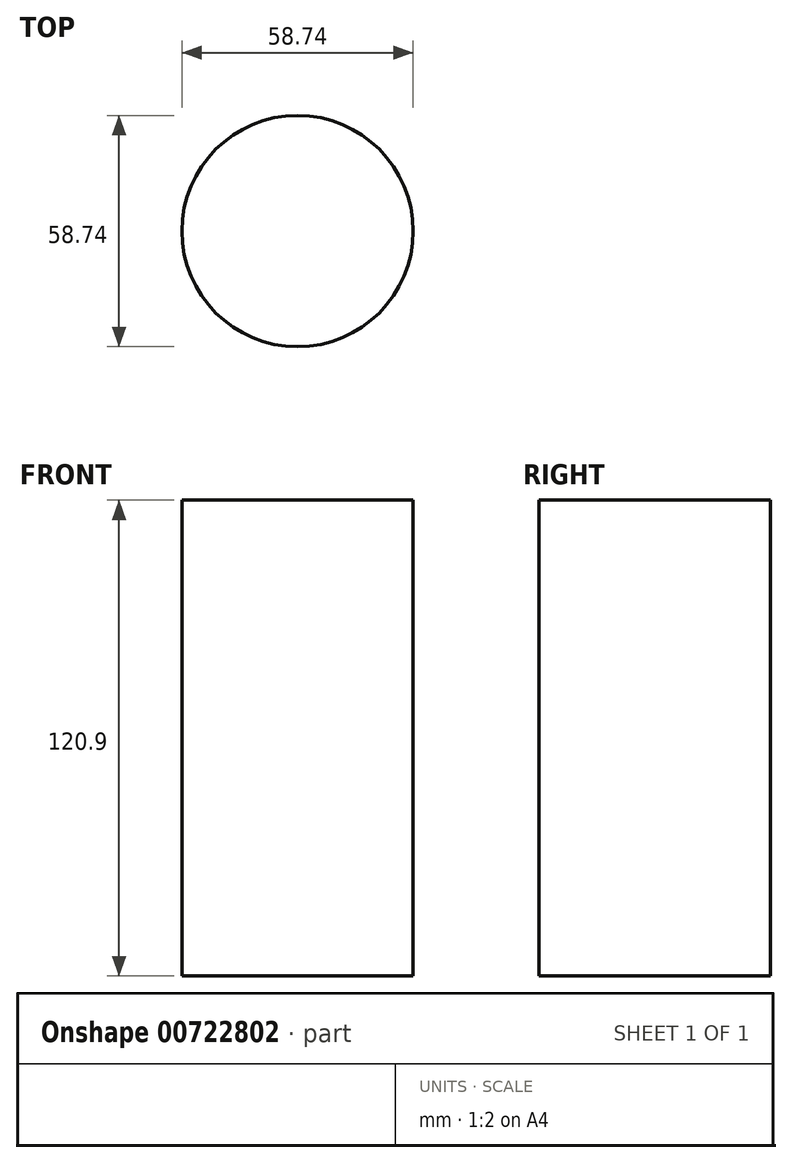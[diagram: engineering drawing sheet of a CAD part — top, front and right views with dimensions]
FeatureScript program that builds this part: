
annotation { "Feature Type Name" : "Feature", "Feature Type Description" : "" }
export const myFeature = defineFeature(function(context is Context, id is Id, definition is map)
    precondition{}
    {
        {
            var Q0;
            Q0=qCreatedBy(makeId("Top.planeOp"),FACE);
            var sketch = newSketch(context, id + "F0", { "sketchPlane" : qUnion([Q0])});
            skCircle(sketch, "E0", {"center": v(0, 0) * mm, "radius": 29.37 * mm});
            skSolve(sketch);
        }
        {
            var Q0;
            Q0 = qSketchRegion(id + "F0", true);
            extrude(context, id + "F1", {"entities" : qUnion([Q0]), "depth" : 120.9 * mm, "offsetDistance" : 25.4 * mm});
        }
    });
